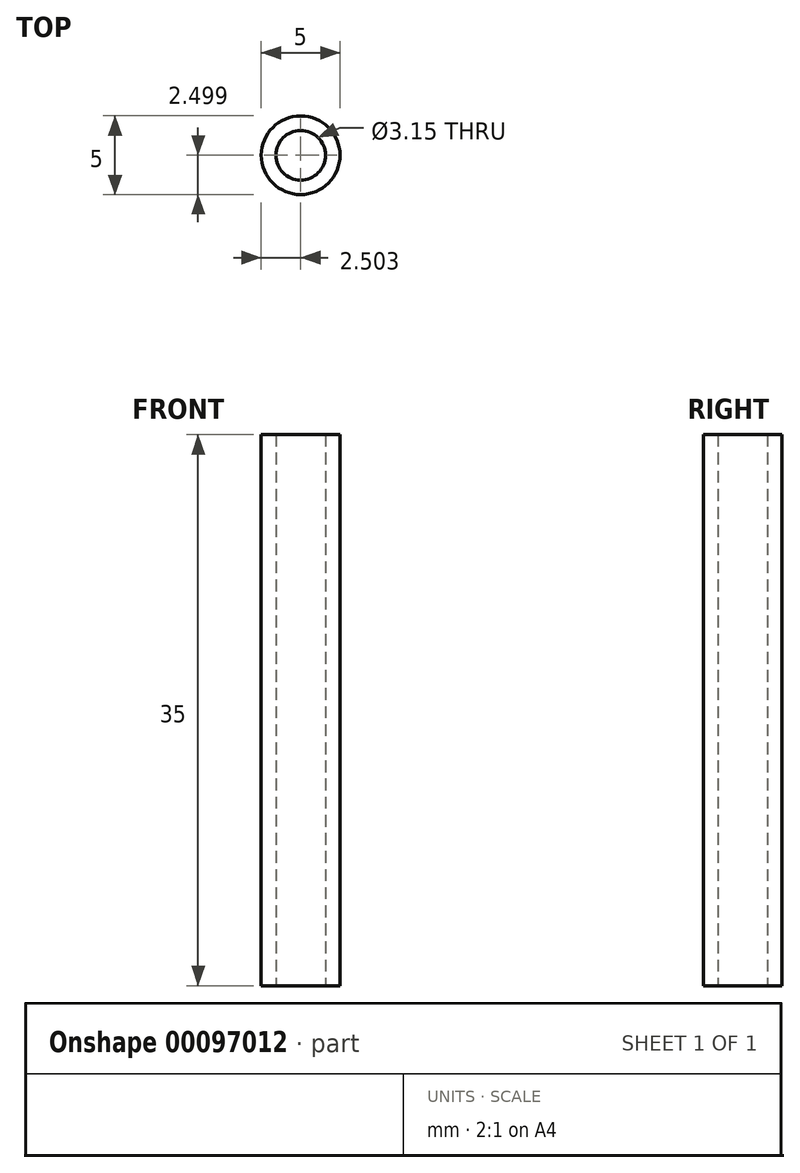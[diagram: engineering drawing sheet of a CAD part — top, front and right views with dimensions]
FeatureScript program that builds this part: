
annotation { "Feature Type Name" : "Feature", "Feature Type Description" : "" }
export const myFeature = defineFeature(function(context is Context, id is Id, definition is map)
    precondition{}
    {
        {
            var Q0;
            Q0=qCreatedBy(makeId("Top.planeOp"),FACE);
            var sketch = newSketch(context, id + "F0", { "sketchPlane" : qUnion([Q0])});
            skCircle(sketch, "E0", {"center": v(-51.02, 31.59) * mm, "radius": 2.5 * mm});
            skCircle(sketch, "E1", {"center": v(-51.02, 31.59) * mm, "radius": 1.57 * mm});
            skSolve(sketch);
        }
        {
            var Q0;
            Q0 = qSketchRegion(id + "F0", true);
            extrude(context, id + "F1", {"entities" : qUnion([Q0]), "depth" : 35 * mm});
        }
    });
